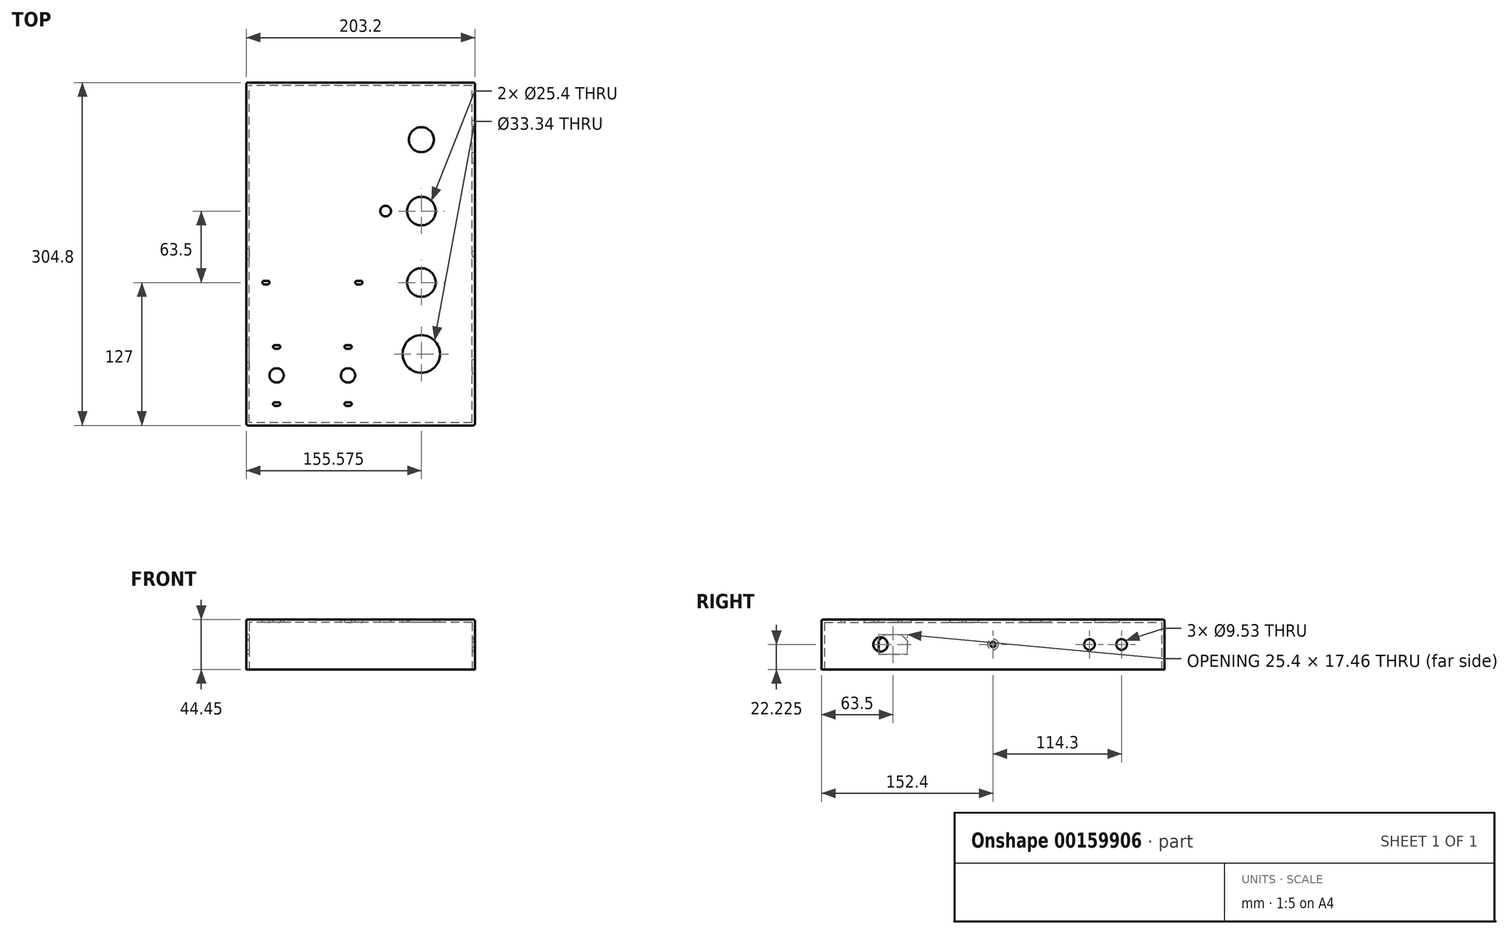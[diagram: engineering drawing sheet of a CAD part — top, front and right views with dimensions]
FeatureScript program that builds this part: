
annotation { "Feature Type Name" : "Feature", "Feature Type Description" : "" }
export const myFeature = defineFeature(function(context is Context, id is Id, definition is map)
    precondition{}
    {
        {
            var Q0;
            Q0=qCreatedBy(makeId("Top.planeOp"),FACE);
            var sketch = newSketch(context, id + "F0", { "sketchPlane" : qUnion([Q0])});
            skLineSegment(sketch, "E0.bottom", {"start": v(101.6, -152.4) * mm, "end": v(-101.6, -152.4) * mm});
            skLineSegment(sketch, "E0.top", {"start": v(101.6, 152.4) * mm, "end": v(-101.6, 152.4) * mm});
            skLineSegment(sketch, "E0.left", {"start": v(101.6, -152.4) * mm, "end": v(101.6, 152.4) * mm});
            skLineSegment(sketch, "E0.right", {"start": v(-101.6, -152.4) * mm, "end": v(-101.6, 152.4) * mm});
            skPoint(sketch, "E0.middle", {"position": v(0, 0) * mm});
            skSolve(sketch);
        }
        {
            var Q0;
            Q0=makeQuery(id+"F0.imprint","IMPRINT",FACE,{"disambiguationData":[TD([[makeQuery(id+"F0.imprint","IMPRINT",EDGE,{"derivedFrom":sQuery(id+"F0.wireOp",EDGE,"E0.bottom")}),-1.0]])]});
            extrude(context, id + "F1", {"entities" : qUnion([Q0]), "depth" : 44.45 * mm});
        }
        {
            var Q0;
            Q0=makeQuery(id+"F1.opExtrude","CAP_FACE",FACE,{"disambiguationData":[OSD([sQuery(id+"F0.wireOp",EDGE,"E0.bottom"),sQuery(id+"F0.wireOp",EDGE,"E0.top"),sQuery(id+"F0.wireOp",EDGE,"E0.left"),sQuery(id+"F0.wireOp",EDGE,"E0.right")])],"isStart":true});
            shell(context, id + "F2", {"entities" : qUnion([Q0]), "thickness" : 2.54 * mm});
        }
        {
            var Q0;
            Q0=makeQuery(id+"F1.opExtrude","CAP_FACE",FACE,{"disambiguationData":[OSD([sQuery(id+"F0.wireOp",EDGE,"E0.bottom"),sQuery(id+"F0.wireOp",EDGE,"E0.top"),sQuery(id+"F0.wireOp",EDGE,"E0.left"),sQuery(id+"F0.wireOp",EDGE,"E0.right")])],"isStart":false});
            var sketch = newSketch(context, id + "F3", { "sketchPlane" : qUnion([Q0])});
            skLineSegment(sketch, "E1.bottom", {"start": v(-3.17, -139.7) * mm, "end": v(-82.55, -139.7) * mm, "construction": true});
            skLineSegment(sketch, "E1.top", {"start": v(-3.18, -76.2) * mm, "end": v(-82.55, -76.2) * mm, "construction": true});
            skLineSegment(sketch, "E1.left", {"start": v(-3.17, -139.7) * mm, "end": v(-3.18, -76.2) * mm, "construction": true});
            skLineSegment(sketch, "E1.right", {"start": v(-82.55, -139.7) * mm, "end": v(-82.55, -76.2) * mm, "construction": true});
            skPoint(sketch, "E1.middle", {"position": v(-42.86, -107.95) * mm});
            skLineSegment(sketch, "E2.bottom", {"start": v(-11.11, -133.35) * mm, "end": v(-74.61, -133.35) * mm, "construction": true});
            skLineSegment(sketch, "E2.top", {"start": v(-11.11, -82.55) * mm, "end": v(-74.61, -82.55) * mm, "construction": true});
            skLineSegment(sketch, "E2.left", {"start": v(-11.11, -133.35) * mm, "end": v(-11.11, -82.55) * mm, "construction": true});
            skLineSegment(sketch, "E2.right", {"start": v(-74.61, -133.35) * mm, "end": v(-74.61, -82.55) * mm, "construction": true});
            skLineSegment(sketch, "E3.bottom", {"start": v(-71.44, -134.94) * mm, "end": v(-77.79, -134.94) * mm});
            skLineSegment(sketch, "E3.top", {"start": v(-71.44, -131.76) * mm, "end": v(-77.79, -131.76) * mm});
            skLineSegment(sketch, "E3.left", {"start": v(-71.44, -134.94) * mm, "end": v(-71.44, -131.76) * mm});
            skLineSegment(sketch, "E3.right", {"start": v(-77.79, -134.94) * mm, "end": v(-77.79, -131.76) * mm});
            skPoint(sketch, "E3.middle", {"position": v(-74.61, -133.35) * mm});
            skLineSegment(sketch, "E4.bottom", {"start": v(-14.29, -84.14) * mm, "end": v(-7.94, -84.14) * mm});
            skLineSegment(sketch, "E4.top", {"start": v(-14.29, -80.96) * mm, "end": v(-7.94, -80.96) * mm});
            skLineSegment(sketch, "E4.left", {"start": v(-14.29, -84.14) * mm, "end": v(-14.29, -80.96) * mm});
            skLineSegment(sketch, "E4.right", {"start": v(-7.94, -84.14) * mm, "end": v(-7.94, -80.96) * mm});
            skPoint(sketch, "E4.middle", {"position": v(-11.11, -82.55) * mm});
            skLineSegment(sketch, "E5.bottom", {"start": v(-14.29, -131.76) * mm, "end": v(-7.94, -131.76) * mm});
            skLineSegment(sketch, "E5.top", {"start": v(-14.29, -134.94) * mm, "end": v(-7.94, -134.94) * mm});
            skLineSegment(sketch, "E5.left", {"start": v(-14.29, -131.76) * mm, "end": v(-14.29, -134.94) * mm});
            skLineSegment(sketch, "E5.right", {"start": v(-7.94, -131.76) * mm, "end": v(-7.94, -134.94) * mm});
            skPoint(sketch, "E5.middle", {"position": v(-11.11, -133.35) * mm});
            skLineSegment(sketch, "E6.bottom", {"start": v(-71.44, -84.14) * mm, "end": v(-77.79, -84.14) * mm});
            skLineSegment(sketch, "E6.top", {"start": v(-71.44, -80.96) * mm, "end": v(-77.79, -80.96) * mm});
            skLineSegment(sketch, "E6.left", {"start": v(-71.44, -84.14) * mm, "end": v(-71.44, -80.96) * mm});
            skLineSegment(sketch, "E6.right", {"start": v(-77.79, -84.14) * mm, "end": v(-77.79, -80.96) * mm});
            skPoint(sketch, "E6.middle", {"position": v(-74.61, -82.55) * mm});
            skPoint(sketch, "E7", {"position": v(-74.61, -107.95) * mm});
            skPoint(sketch, "E8", {"position": v(-11.11, -107.95) * mm});
            skSolve(sketch);
        }
        {
            var Q0;
            Q0=makeQuery(id+"F3.imprint","IMPRINT",FACE,{"disambiguationData":[TD([[makeQuery(id+"F3.imprint","IMPRINT",EDGE,{"derivedFrom":sQuery(id+"F3.wireOp",EDGE,"E3.bottom")}),-1.0]])]});
            var Q1;
            Q1=makeQuery(id+"F3.imprint","IMPRINT",FACE,{"disambiguationData":[TD([[makeQuery(id+"F3.imprint","IMPRINT",EDGE,{"derivedFrom":sQuery(id+"F3.wireOp",EDGE,"E6.bottom")}),-1.0]])]});
            var Q2;
            Q2=makeQuery(id+"F3.imprint","IMPRINT",FACE,{"disambiguationData":[TD([[makeQuery(id+"F3.imprint","IMPRINT",EDGE,{"derivedFrom":sQuery(id+"F3.wireOp",EDGE,"E4.bottom")}),1.0]])]});
            var Q3;
            Q3=makeQuery(id+"F3.imprint","IMPRINT",FACE,{"disambiguationData":[TD([[makeQuery(id+"F3.imprint","IMPRINT",EDGE,{"derivedFrom":sQuery(id+"F3.wireOp",EDGE,"E5.bottom")}),-1.0]])]});
            extrude(context, id + "F4", {"entities" : qUnion([Q0, Q1, Q2, Q3]), "operationType" : NewBodyOperationType.REMOVE, "oppositeDirection" : true, "depth" : 25.4 * mm});
        }
        {
            var Q0;
            Q0=makeQuery(id+"F4.boolean.opBoolean","COPY",EDGE,{"derivedFrom":makeQuery(id+"F4.opExtrude","SWEPT_EDGE",EDGE,{"disambiguationData":[OSD([sQuery(id+"F3.wireOp",EDGE,"E3.top"),sQuery(id+"F3.wireOp",EDGE,"E3.right")])]})});
            var Q1;
            Q1=makeQuery(id+"F4.boolean.opBoolean","COPY",EDGE,{"derivedFrom":makeQuery(id+"F4.opExtrude","SWEPT_EDGE",EDGE,{"disambiguationData":[OSD([sQuery(id+"F3.wireOp",EDGE,"E5.bottom"),sQuery(id+"F3.wireOp",EDGE,"E5.left")])]})});
            var Q2;
            Q2=makeQuery(id+"F4.boolean.opBoolean","COPY",EDGE,{"derivedFrom":makeQuery(id+"F4.opExtrude","SWEPT_EDGE",EDGE,{"disambiguationData":[OSD([sQuery(id+"F3.wireOp",EDGE,"E6.top"),sQuery(id+"F3.wireOp",EDGE,"E6.right")])]})});
            var Q3;
            Q3=makeQuery(id+"F4.boolean.opBoolean","COPY",EDGE,{"derivedFrom":makeQuery(id+"F4.opExtrude","SWEPT_EDGE",EDGE,{"disambiguationData":[OSD([sQuery(id+"F3.wireOp",EDGE,"E6.top"),sQuery(id+"F3.wireOp",EDGE,"E6.left")])]})});
            var Q4;
            Q4=makeQuery(id+"F4.boolean.opBoolean","COPY",EDGE,{"derivedFrom":makeQuery(id+"F4.opExtrude","SWEPT_EDGE",EDGE,{"disambiguationData":[OSD([sQuery(id+"F3.wireOp",EDGE,"E4.top"),sQuery(id+"F3.wireOp",EDGE,"E4.right")])]})});
            var Q5;
            Q5=makeQuery(id+"F4.boolean.opBoolean","COPY",EDGE,{"derivedFrom":makeQuery(id+"F4.opExtrude","SWEPT_EDGE",EDGE,{"disambiguationData":[OSD([sQuery(id+"F3.wireOp",EDGE,"E5.bottom"),sQuery(id+"F3.wireOp",EDGE,"E5.right")])]})});
            var Q6;
            Q6=makeQuery(id+"F4.boolean.opBoolean","COPY",EDGE,{"derivedFrom":makeQuery(id+"F4.opExtrude","SWEPT_EDGE",EDGE,{"disambiguationData":[OSD([sQuery(id+"F3.wireOp",EDGE,"E3.top"),sQuery(id+"F3.wireOp",EDGE,"E3.left")])]})});
            var Q7;
            Q7=makeQuery(id+"F4.boolean.opBoolean","COPY",EDGE,{"derivedFrom":makeQuery(id+"F4.opExtrude","SWEPT_EDGE",EDGE,{"disambiguationData":[OSD([sQuery(id+"F3.wireOp",EDGE,"E5.top"),sQuery(id+"F3.wireOp",EDGE,"E5.left")])]})});
            var Q8;
            Q8=makeQuery(id+"F4.boolean.opBoolean","COPY",EDGE,{"derivedFrom":makeQuery(id+"F4.opExtrude","SWEPT_EDGE",EDGE,{"disambiguationData":[OSD([sQuery(id+"F3.wireOp",EDGE,"E3.bottom"),sQuery(id+"F3.wireOp",EDGE,"E3.right")])]})});
            var Q9;
            Q9=makeQuery(id+"F4.boolean.opBoolean","COPY",EDGE,{"derivedFrom":makeQuery(id+"F4.opExtrude","SWEPT_EDGE",EDGE,{"disambiguationData":[OSD([sQuery(id+"F3.wireOp",EDGE,"E6.bottom"),sQuery(id+"F3.wireOp",EDGE,"E6.right")])]})});
            var Q10;
            Q10=makeQuery(id+"F4.boolean.opBoolean","COPY",EDGE,{"derivedFrom":makeQuery(id+"F4.opExtrude","SWEPT_EDGE",EDGE,{"disambiguationData":[OSD([sQuery(id+"F3.wireOp",EDGE,"E4.bottom"),sQuery(id+"F3.wireOp",EDGE,"E4.left")])]})});
            var Q11;
            Q11=makeQuery(id+"F4.boolean.opBoolean","COPY",EDGE,{"derivedFrom":makeQuery(id+"F4.opExtrude","SWEPT_EDGE",EDGE,{"disambiguationData":[OSD([sQuery(id+"F3.wireOp",EDGE,"E5.top"),sQuery(id+"F3.wireOp",EDGE,"E5.right")])]})});
            var Q12;
            Q12=makeQuery(id+"F4.boolean.opBoolean","COPY",EDGE,{"derivedFrom":makeQuery(id+"F4.opExtrude","SWEPT_EDGE",EDGE,{"disambiguationData":[OSD([sQuery(id+"F3.wireOp",EDGE,"E4.bottom"),sQuery(id+"F3.wireOp",EDGE,"E4.right")])]})});
            var Q13;
            Q13=makeQuery(id+"F4.boolean.opBoolean","COPY",EDGE,{"derivedFrom":makeQuery(id+"F4.opExtrude","SWEPT_EDGE",EDGE,{"disambiguationData":[OSD([sQuery(id+"F3.wireOp",EDGE,"E6.bottom"),sQuery(id+"F3.wireOp",EDGE,"E6.left")])]})});
            var Q14;
            Q14=makeQuery(id+"F4.boolean.opBoolean","COPY",EDGE,{"derivedFrom":makeQuery(id+"F4.opExtrude","SWEPT_EDGE",EDGE,{"disambiguationData":[OSD([sQuery(id+"F3.wireOp",EDGE,"E3.bottom"),sQuery(id+"F3.wireOp",EDGE,"E3.left")])]})});
            var Q15;
            Q15=makeQuery(id+"F4.boolean.opBoolean","COPY",EDGE,{"derivedFrom":makeQuery(id+"F4.opExtrude","SWEPT_EDGE",EDGE,{"disambiguationData":[OSD([sQuery(id+"F3.wireOp",EDGE,"E4.top"),sQuery(id+"F3.wireOp",EDGE,"E4.left")])]})});
            fillet(context, id + "F5", {"entities" : qUnion([Q0, Q1, Q2, Q3, Q4, Q5, Q6, Q7, Q8, Q9, Q10, Q11, Q12, Q13, Q14, Q15]), "radius" : 1.59 * mm, "tangentPropagation" : true, "allowEdgeOverflow" : false});
        }
        {
            var Q0;
            Q0=makeQuery(id+"F1.opExtrude","CAP_FACE",FACE,{"disambiguationData":[OSD([sQuery(id+"F0.wireOp",EDGE,"E0.bottom"),sQuery(id+"F0.wireOp",EDGE,"E0.top"),sQuery(id+"F0.wireOp",EDGE,"E0.left"),sQuery(id+"F0.wireOp",EDGE,"E0.right")])],"isStart":false});
            var sketch = newSketch(context, id + "F6", { "sketchPlane" : qUnion([Q0])});
            skLineSegment(sketch, "E9", {"start": v(0, 0) * mm, "end": v(53.97, 0) * mm, "construction": true});
            skLineSegment(sketch, "E10", {"start": v(53.97, 0) * mm, "end": v(53.98, -88.9) * mm, "construction": true});
            skCircle(sketch, "E11", {"center": v(53.98, -88.9) * mm, "radius": 16.67 * mm, "construction": true});
            skPoint(sketch, "E12", {"position": v(53.98, -25.4) * mm});
            skLineSegment(sketch, "E13", {"start": v(53.97, 0) * mm, "end": v(53.97, 152.4) * mm, "construction": true});
            skPoint(sketch, "E14", {"position": v(53.97, 38.1) * mm});
            skPoint(sketch, "E15", {"position": v(53.97, 101.6) * mm});
            skLineSegment(sketch, "E16", {"start": v(53.97, 38.1) * mm, "end": v(22.22, 38.1) * mm, "construction": true});
            skPoint(sketch, "E17", {"position": v(22.22, 38.1) * mm});
            skSolve(sketch);
        }
        {
            var Q0;
            Q0=sQuery(id+"F6.wireOp",VERTEX,"E11.center");
            var Q1;
            Q1=makeQuery(id+"F1.opExtrude","SWEPT_BODY",BODY,{"disambiguationData":[OSD([sQuery(id+"F0.wireOp",EDGE,"E0.bottom"),sQuery(id+"F0.wireOp",EDGE,"E0.top"),sQuery(id+"F0.wireOp",EDGE,"E0.left"),sQuery(id+"F0.wireOp",EDGE,"E0.right")])]});
            hole(context, id + "F7", {"style" : HoleStyle.SIMPLE, "endStyle" : HoleEndStyle.BLIND, "holeDiameter" : 33.34 * mm, "holeDepth" : 19.05 * mm, "locations" : qUnion([Q0]), "scope" : qUnion([Q1])});
        }
        {
            var Q0;
            Q0=sQuery(id+"F6.wireOp",VERTEX,"E12");
            var Q1;
            Q1=sQuery(id+"F6.wireOp",VERTEX,"E14");
            var Q2;
            Q2=makeQuery(id+"F1.opExtrude","SWEPT_BODY",BODY,{"disambiguationData":[OSD([sQuery(id+"F0.wireOp",EDGE,"E0.bottom"),sQuery(id+"F0.wireOp",EDGE,"E0.top"),sQuery(id+"F0.wireOp",EDGE,"E0.left"),sQuery(id+"F0.wireOp",EDGE,"E0.right")])]});
            hole(context, id + "F8", {"style" : HoleStyle.SIMPLE, "endStyle" : HoleEndStyle.BLIND, "holeDiameter" : 25.4 * mm, "holeDepth" : 19.05 * mm, "locations" : qUnion([Q0, Q1]), "scope" : qUnion([Q2])});
        }
        {
            var Q0;
            Q0=sQuery(id+"F6.wireOp",VERTEX,"E15");
            var Q1;
            Q1=makeQuery(id+"F1.opExtrude","SWEPT_BODY",BODY,{"disambiguationData":[OSD([sQuery(id+"F0.wireOp",EDGE,"E0.bottom"),sQuery(id+"F0.wireOp",EDGE,"E0.top"),sQuery(id+"F0.wireOp",EDGE,"E0.left"),sQuery(id+"F0.wireOp",EDGE,"E0.right")])]});
            hole(context, id + "F9", {"style" : HoleStyle.SIMPLE, "endStyle" : HoleEndStyle.BLIND, "holeDiameter" : 22.22 * mm, "holeDepth" : 19.05 * mm, "locations" : qUnion([Q0]), "scope" : qUnion([Q1])});
        }
        {
            var Q0;
            Q0=makeQuery(id+"F1.opExtrude","SWEPT_FACE",FACE,{"disambiguationData":[OSD([sQuery(id+"F0.wireOp",EDGE,"E0.left")])]});
            var sketch = newSketch(context, id + "F10", { "sketchPlane" : qUnion([Q0])});
            skLineSegment(sketch, "E18", {"start": v(0, 0) * mm, "end": v(0, 44.45) * mm, "construction": true});
            skPoint(sketch, "E19", {"position": v(0, 22.23) * mm});
            skLineSegment(sketch, "E20", {"start": v(0, 22.23) * mm, "end": v(152.4, 22.23) * mm, "construction": true});
            skPoint(sketch, "E21", {"position": v(85.73, 22.23) * mm});
            skPoint(sketch, "E22", {"position": v(114.3, 22.23) * mm});
            skLineSegment(sketch, "E23", {"start": v(0, 22.23) * mm, "end": v(-152.4, 22.22) * mm, "construction": true});
            skPoint(sketch, "E24", {"position": v(-100.01, 22.22) * mm});
            skSolve(sketch);
        }
        {
            var Q0;
            Q0=sQuery(id+"F10.wireOp",VERTEX,"E19");
            var Q1;
            Q1=makeQuery(id+"F1.opExtrude","SWEPT_BODY",BODY,{"disambiguationData":[OSD([sQuery(id+"F0.wireOp",EDGE,"E0.bottom"),sQuery(id+"F0.wireOp",EDGE,"E0.top"),sQuery(id+"F0.wireOp",EDGE,"E0.left"),sQuery(id+"F0.wireOp",EDGE,"E0.right")])]});
            hole(context, id + "F11", {"style" : HoleStyle.SIMPLE, "endStyle" : HoleEndStyle.BLIND, "holeDiameter" : 4.76 * mm, "holeDepth" : 19.05 * mm, "locations" : qUnion([Q0]), "scope" : qUnion([Q1])});
        }
        {
            var Q0;
            Q0=sQuery(id+"F10.wireOp",VERTEX,"E21");
            var Q1;
            Q1=sQuery(id+"F10.wireOp",VERTEX,"E22");
            var Q2;
            Q2=makeQuery(id+"F1.opExtrude","SWEPT_BODY",BODY,{"disambiguationData":[OSD([sQuery(id+"F0.wireOp",EDGE,"E0.bottom"),sQuery(id+"F0.wireOp",EDGE,"E0.top"),sQuery(id+"F0.wireOp",EDGE,"E0.left"),sQuery(id+"F0.wireOp",EDGE,"E0.right")])]});
            hole(context, id + "F12", {"style" : HoleStyle.SIMPLE, "endStyle" : HoleEndStyle.BLIND, "holeDiameter" : 9.52 * mm, "holeDepth" : 19.05 * mm, "locations" : qUnion([Q0, Q1]), "scope" : qUnion([Q2])});
        }
        {
            var Q0;
            Q0=sQuery(id+"F10.wireOp",VERTEX,"E24");
            var Q1;
            Q1=makeQuery(id+"F1.opExtrude","SWEPT_BODY",BODY,{"disambiguationData":[OSD([sQuery(id+"F0.wireOp",EDGE,"E0.bottom"),sQuery(id+"F0.wireOp",EDGE,"E0.top"),sQuery(id+"F0.wireOp",EDGE,"E0.left"),sQuery(id+"F0.wireOp",EDGE,"E0.right")])]});
            hole(context, id + "F13", {"style" : HoleStyle.SIMPLE, "endStyle" : HoleEndStyle.BLIND, "holeDiameter" : 12.7 * mm, "holeDepth" : 19.05 * mm, "locations" : qUnion([Q0]), "scope" : qUnion([Q1])});
        }
        {
            var Q0;
            Q0=makeQuery(id+"F1.opExtrude","SWEPT_FACE",FACE,{"disambiguationData":[OSD([sQuery(id+"F0.wireOp",EDGE,"E0.right")])]});
            var sketch = newSketch(context, id + "F14", { "sketchPlane" : qUnion([Q0])});
            skLineSegment(sketch, "E25", {"start": v(0, 22.23) * mm, "end": v(88.9, 22.23) * mm, "construction": true});
            skLineSegment(sketch, "E26.bottom", {"start": v(101.6, 30.96) * mm, "end": v(76.2, 30.96) * mm});
            skLineSegment(sketch, "E26.top", {"start": v(101.6, 13.5) * mm, "end": v(76.2, 13.5) * mm});
            skLineSegment(sketch, "E26.left", {"start": v(101.6, 30.96) * mm, "end": v(101.6, 13.5) * mm});
            skLineSegment(sketch, "E26.right", {"start": v(76.2, 30.96) * mm, "end": v(76.2, 13.5) * mm});
            skPoint(sketch, "E26.middle", {"position": v(88.9, 22.23) * mm});
            skLineSegment(sketch, "E27", {"start": v(88.9, 13.5) * mm, "end": v(88.9, 30.96) * mm, "construction": true});
            skLineSegment(sketch, "E28", {"start": v(81.56, 13.5) * mm, "end": v(76.2, 18.85) * mm});
            skLineSegment(sketch, "E29.MirrorCS", {"start": v(96.24, 13.5) * mm, "end": v(101.6, 18.85) * mm});
            skLineSegment(sketch, "E30", {"start": v(0, 0) * mm, "end": v(0, 44.45) * mm, "construction": true});
            skLineSegment(sketch, "E31.MirrorCS", {"start": v(-81.56, 13.5) * mm, "end": v(-76.2, 18.85) * mm});
            skLineSegment(sketch, "E32.MirrorCS", {"start": v(-96.24, 13.5) * mm, "end": v(-101.6, 18.85) * mm});
            skLineSegment(sketch, "E33.MirrorCS", {"start": v(0, 22.23) * mm, "end": v(-88.9, 22.22) * mm, "construction": true});
            skLineSegment(sketch, "E34.MirrorCS", {"start": v(-101.6, 30.96) * mm, "end": v(-76.2, 30.96) * mm});
            skLineSegment(sketch, "E35.MirrorCS", {"start": v(-101.6, 13.5) * mm, "end": v(-76.2, 13.5) * mm});
            skLineSegment(sketch, "E36.MirrorCS", {"start": v(-101.6, 30.96) * mm, "end": v(-101.6, 13.5) * mm});
            skPoint(sketch, "E37.MirrorP", {"position": v(-88.9, 22.23) * mm});
            skLineSegment(sketch, "E38.MirrorCS", {"start": v(-88.9, 13.5) * mm, "end": v(-88.9, 30.96) * mm, "construction": true});
            skLineSegment(sketch, "E39.MirrorCS", {"start": v(-76.2, 30.96) * mm, "end": v(-76.2, 13.5) * mm});
            skLineSegment(sketch, "E40.MirrorCS", {"start": v(81.56, 30.96) * mm, "end": v(76.2, 25.6) * mm});
            skLineSegment(sketch, "E41.MirrorCS", {"start": v(96.24, 30.96) * mm, "end": v(101.6, 25.6) * mm});
            skSolve(sketch);
        }
        {
            var Q0;
            {var subQ0=sQuery(id+"F14.wireOp",EDGE,"E28");Q0=makeQuery(id+"F14.imprint","IMPRINT",FACE,{"disambiguationData":[TD([[makeQuery(id+"F14.imprint","IMPRINT",EDGE,{"derivedFrom":subQ0}),-1.0]])]});}
            var Q1;
            {var subQ3=sQuery(id+"F14.wireOp",EDGE,"E28");Q1=makeQuery(id+"F14.imprint","IMPRINT",FACE,{"disambiguationData":[TD([[makeQuery(id+"F14.imprint","IMPRINT",EDGE,{"derivedFrom":subQ3}),1.0]])]});}
            var Q2;
            {var subQ3=sQuery(id+"F14.wireOp",EDGE,"E29.MirrorCS");Q2=makeQuery(id+"F14.imprint","IMPRINT",FACE,{"disambiguationData":[TD([[makeQuery(id+"F14.imprint","IMPRINT",EDGE,{"derivedFrom":subQ3}),-1.0]])]});}
            extrude(context, id + "F15", {"entities" : qUnion([Q0, Q1, Q2]), "operationType" : NewBodyOperationType.REMOVE, "oppositeDirection" : true, "depth" : 25.4 * mm});
        }
        {
            var Q0;
            Q0=sQuery(id+"F3.wireOp",VERTEX,"E7");
            var Q1;
            Q1=sQuery(id+"F3.wireOp",VERTEX,"E8");
            var Q2;
            Q2=makeQuery(id+"F1.opExtrude","SWEPT_BODY",BODY,{"disambiguationData":[OSD([sQuery(id+"F0.wireOp",EDGE,"E0.bottom"),sQuery(id+"F0.wireOp",EDGE,"E0.top"),sQuery(id+"F0.wireOp",EDGE,"E0.left"),sQuery(id+"F0.wireOp",EDGE,"E0.right")])]});
            hole(context, id + "F16", {"style" : HoleStyle.SIMPLE, "endStyle" : HoleEndStyle.BLIND, "holeDiameter" : 12.7 * mm, "holeDepth" : 19.05 * mm, "locations" : qUnion([Q0, Q1]), "scope" : qUnion([Q2])});
        }
        {
            var Q0;
            Q0=makeQuery(id+"F3.imprint","IMPRINT",FACE,{"disambiguationData":[TD([[makeQuery(id+"F3.imprint","IMPRINT",EDGE,{"derivedFrom":sQuery(id+"F3.wireOp",EDGE,"E3.bottom")}),1.0]])]});
            var sketch = newSketch(context, id + "F17", { "sketchPlane" : qUnion([Q0])});
            skLineSegment(sketch, "E42", {"start": v(-42.86, -107.95) * mm, "end": v(-42.86, -76.2) * mm, "construction": true});
            skLineSegment(sketch, "E43", {"start": v(-42.86, -76.2) * mm, "end": v(-42.86, -25.4) * mm, "construction": true});
            skLineSegment(sketch, "E44", {"start": v(-84.14, -25.4) * mm, "end": v(-1.59, -25.4) * mm, "construction": true});
            skLineSegment(sketch, "E45.bottom", {"start": v(-80.96, -26.99) * mm, "end": v(-87.31, -26.99) * mm});
            skLineSegment(sketch, "E45.top", {"start": v(-80.96, -23.81) * mm, "end": v(-87.31, -23.81) * mm});
            skLineSegment(sketch, "E45.left", {"start": v(-80.96, -26.99) * mm, "end": v(-80.96, -23.81) * mm});
            skLineSegment(sketch, "E45.right", {"start": v(-87.31, -26.99) * mm, "end": v(-87.31, -23.81) * mm});
            skPoint(sketch, "E45.middle", {"position": v(-84.14, -25.4) * mm});
            skLineSegment(sketch, "E46.bottom", {"start": v(1.59, -26.99) * mm, "end": v(-4.76, -26.99) * mm});
            skLineSegment(sketch, "E46.top", {"start": v(1.59, -23.81) * mm, "end": v(-4.76, -23.81) * mm});
            skLineSegment(sketch, "E46.left", {"start": v(1.59, -26.99) * mm, "end": v(1.59, -23.81) * mm});
            skLineSegment(sketch, "E46.right", {"start": v(-4.76, -26.99) * mm, "end": v(-4.76, -23.81) * mm});
            skPoint(sketch, "E46.middle", {"position": v(-1.59, -25.4) * mm});
            skSolve(sketch);
        }
        {
            var Q0;
            Q0=makeQuery(id+"F17.imprint","IMPRINT",FACE,{"disambiguationData":[TD([[makeQuery(id+"F17.imprint","IMPRINT",EDGE,{"derivedFrom":sQuery(id+"F17.wireOp",EDGE,"E45.bottom")}),-1.0]])]});
            var Q1;
            Q1=makeQuery(id+"F17.imprint","IMPRINT",FACE,{"disambiguationData":[TD([[makeQuery(id+"F17.imprint","IMPRINT",EDGE,{"derivedFrom":sQuery(id+"F17.wireOp",EDGE,"E46.bottom")}),-1.0]])]});
            extrude(context, id + "F18", {"entities" : qUnion([Q0, Q1]), "operationType" : NewBodyOperationType.REMOVE, "oppositeDirection" : true, "depth" : 25.4 * mm});
        }
        {
            var Q0;
            Q0=makeQuery(id+"F18.boolean.opBoolean","COPY",EDGE,{"derivedFrom":makeQuery(id+"F18.opExtrude","SWEPT_EDGE",EDGE,{"disambiguationData":[OSD([sQuery(id+"F17.wireOp",EDGE,"E45.top"),sQuery(id+"F17.wireOp",EDGE,"E45.right")])]})});
            var Q1;
            Q1=makeQuery(id+"F18.boolean.opBoolean","COPY",EDGE,{"derivedFrom":makeQuery(id+"F18.opExtrude","SWEPT_EDGE",EDGE,{"disambiguationData":[OSD([sQuery(id+"F17.wireOp",EDGE,"E46.top"),sQuery(id+"F17.wireOp",EDGE,"E46.right")])]})});
            var Q2;
            Q2=makeQuery(id+"F18.boolean.opBoolean","COPY",EDGE,{"derivedFrom":makeQuery(id+"F18.opExtrude","SWEPT_EDGE",EDGE,{"disambiguationData":[OSD([sQuery(id+"F17.wireOp",EDGE,"E45.top"),sQuery(id+"F17.wireOp",EDGE,"E45.left")])]})});
            var Q3;
            Q3=makeQuery(id+"F18.boolean.opBoolean","COPY",EDGE,{"derivedFrom":makeQuery(id+"F18.opExtrude","SWEPT_EDGE",EDGE,{"disambiguationData":[OSD([sQuery(id+"F17.wireOp",EDGE,"E46.top"),sQuery(id+"F17.wireOp",EDGE,"E46.left")])]})});
            var Q4;
            Q4=makeQuery(id+"F18.boolean.opBoolean","COPY",EDGE,{"derivedFrom":makeQuery(id+"F18.opExtrude","SWEPT_EDGE",EDGE,{"disambiguationData":[OSD([sQuery(id+"F17.wireOp",EDGE,"E45.bottom"),sQuery(id+"F17.wireOp",EDGE,"E45.right")])]})});
            var Q5;
            Q5=makeQuery(id+"F18.boolean.opBoolean","COPY",EDGE,{"derivedFrom":makeQuery(id+"F18.opExtrude","SWEPT_EDGE",EDGE,{"disambiguationData":[OSD([sQuery(id+"F17.wireOp",EDGE,"E46.bottom"),sQuery(id+"F17.wireOp",EDGE,"E46.right")])]})});
            var Q6;
            Q6=makeQuery(id+"F18.boolean.opBoolean","COPY",EDGE,{"derivedFrom":makeQuery(id+"F18.opExtrude","SWEPT_EDGE",EDGE,{"disambiguationData":[OSD([sQuery(id+"F17.wireOp",EDGE,"E45.bottom"),sQuery(id+"F17.wireOp",EDGE,"E45.left")])]})});
            var Q7;
            Q7=makeQuery(id+"F18.boolean.opBoolean","COPY",EDGE,{"derivedFrom":makeQuery(id+"F18.opExtrude","SWEPT_EDGE",EDGE,{"disambiguationData":[OSD([sQuery(id+"F17.wireOp",EDGE,"E46.bottom"),sQuery(id+"F17.wireOp",EDGE,"E46.left")])]})});
            fillet(context, id + "F19", {"entities" : qUnion([Q0, Q1, Q2, Q3, Q4, Q5, Q6, Q7]), "radius" : 1.59 * mm, "tangentPropagation" : true, "allowEdgeOverflow" : false});
        }
        {
            var Q0;
            Q0=sQuery(id+"F14.wireOp",VERTEX,"E33.MirrorCS.start");
            var Q1;
            Q1=makeQuery(id+"F1.opExtrude","SWEPT_BODY",BODY,{"disambiguationData":[OSD([sQuery(id+"F0.wireOp",EDGE,"E0.bottom"),sQuery(id+"F0.wireOp",EDGE,"E0.top"),sQuery(id+"F0.wireOp",EDGE,"E0.left"),sQuery(id+"F0.wireOp",EDGE,"E0.right")])]});
            hole(context, id + "F20", {"style" : HoleStyle.SIMPLE, "endStyle" : HoleEndStyle.BLIND, "holeDiameter" : 9.52 * mm, "holeDepth" : 5.7 * mm, "locations" : qUnion([Q0]), "scope" : qUnion([Q1])});
        }
        {
            var Q0;
            Q0=sQuery(id+"F6.wireOp",VERTEX,"E17");
            var Q1;
            Q1=makeQuery(id+"F1.opExtrude","SWEPT_BODY",BODY,{"disambiguationData":[OSD([sQuery(id+"F0.wireOp",EDGE,"E0.bottom"),sQuery(id+"F0.wireOp",EDGE,"E0.top"),sQuery(id+"F0.wireOp",EDGE,"E0.left"),sQuery(id+"F0.wireOp",EDGE,"E0.right")])]});
            hole(context, id + "F21", {"style" : HoleStyle.SIMPLE, "endStyle" : HoleEndStyle.BLIND, "holeDiameter" : 9.52 * mm, "holeDepth" : 5.7 * mm, "locations" : qUnion([Q0]), "scope" : qUnion([Q1])});
        }
        {
            var Q0;
            Q0=makeQuery(id+"F1.opExtrude","CAP_EDGE",EDGE,{"disambiguationData":[OSD([sQuery(id+"F0.wireOp",EDGE,"E0.bottom")])],"isStart":false});
            var Q1;
            Q1=makeQuery(id+"F1.opExtrude","CAP_EDGE",EDGE,{"disambiguationData":[OSD([sQuery(id+"F0.wireOp",EDGE,"E0.left")])],"isStart":false});
            var Q2;
            Q2=makeQuery(id+"F1.opExtrude","SWEPT_EDGE",EDGE,{"disambiguationData":[OSD([sQuery(id+"F0.wireOp",EDGE,"E0.bottom"),sQuery(id+"F0.wireOp",EDGE,"E0.left")])]});
            var Q3;
            Q3=makeQuery(id+"F1.opExtrude","CAP_EDGE",EDGE,{"disambiguationData":[OSD([sQuery(id+"F0.wireOp",EDGE,"E0.top")])],"isStart":false});
            var Q4;
            Q4=makeQuery(id+"F1.opExtrude","SWEPT_EDGE",EDGE,{"disambiguationData":[OSD([sQuery(id+"F0.wireOp",EDGE,"E0.top"),sQuery(id+"F0.wireOp",EDGE,"E0.left")])]});
            var Q5;
            Q5=makeQuery(id+"F1.opExtrude","SWEPT_EDGE",EDGE,{"disambiguationData":[OSD([sQuery(id+"F0.wireOp",EDGE,"E0.top"),sQuery(id+"F0.wireOp",EDGE,"E0.right")])]});
            var Q6;
            Q6=makeQuery(id+"F1.opExtrude","CAP_EDGE",EDGE,{"disambiguationData":[OSD([sQuery(id+"F0.wireOp",EDGE,"E0.right")])],"isStart":false});
            var Q7;
            Q7=makeQuery(id+"F1.opExtrude","SWEPT_EDGE",EDGE,{"disambiguationData":[OSD([sQuery(id+"F0.wireOp",EDGE,"E0.bottom"),sQuery(id+"F0.wireOp",EDGE,"E0.right")])]});
            fillet(context, id + "F22", {"entities" : qUnion([Q0, Q1, Q2, Q3, Q4, Q5, Q6, Q7]), "radius" : 1.59 * mm, "tangentPropagation" : true, "allowEdgeOverflow" : false});
        }
    });
